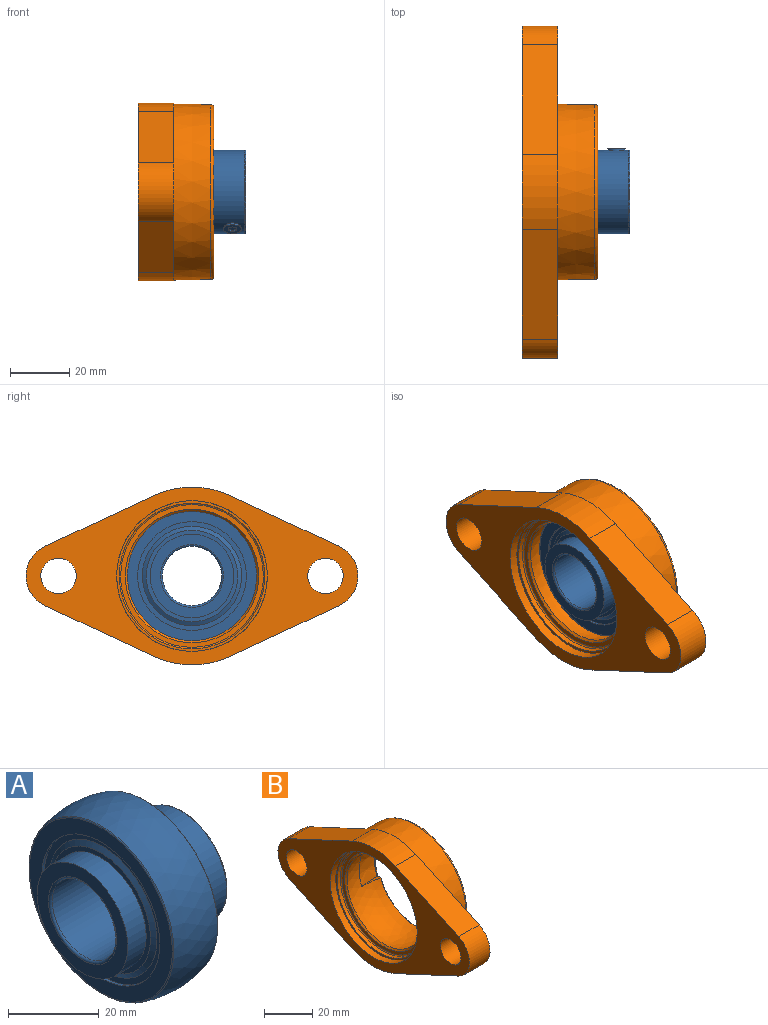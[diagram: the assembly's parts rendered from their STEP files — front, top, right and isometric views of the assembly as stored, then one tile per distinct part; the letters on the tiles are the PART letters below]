
ASSEMBLY  parts=2 mates=1
PART A: 39 faces, bbox 31x48.7x48.7 mm
  f0: cylinder r=3mm len=6mm, axis (0,-0.5,-0.87), area 13.8mm2, adj f15,f21
  f1: plane 30.85x30.85mm, normal (-1,0,0), area 122.9mm2, adj f2,f16
  f2: cone r=16.75mm half-angle=62.2deg, axis (1,0,0), area 151.5mm2, adj f1,f3
  f3: plane 36.68x36.68mm, normal (-1,0,0), area 175mm2, adj f2,f4
  f4: cylinder r=18.34mm len=36.68mm, axis (-1,0,0), area 80.7mm2, adj f3,f5
  f5: plane 44.42x44.42mm, normal (-1,0,0), area 493.5mm2, adj f4,f6
  f6: torus R=22.21mm, axis (1,0,0), area 53.9mm2, adj f5,f7
  f7: sphere r=23.5mm, area 2004.2mm2, adj f6,f8
  f8: torus R=22.21mm, axis (1,0,0), area 53.9mm2, adj f7,f9
  f9: plane 44.42x44.42mm, normal (1,0,0), area 493.5mm2, adj f8,f10
  f10: cylinder r=18.34mm len=36.68mm, axis (-1,0,0), area 80.7mm2, adj f9,f11
  f11: plane 36.68x36.68mm, normal (1,0,0), area 175mm2, adj f10,f12
  f12: cone r=15.42mm half-angle=62.2deg, axis (-1,0,0), area 151.5mm2, adj f11,f13
  f13: plane 30.85x30.85mm, normal (1,0,0), area 122.9mm2, adj f12,f15
  f14: torus R=13.8mm, axis (1,0,0), area 41.4mm2, adj f15,f37
  f15: cylinder r=14.1mm len=28.2mm, axis (-1,0,0), area 911.4mm2, adj f0,f13,f14,f38
  f16: cylinder r=14.1mm len=28.2mm, axis (-1,0,0), area 505mm2, adj f1,f33
  f17: cylinder r=14.1mm len=3mm, axis (-1,0,0), area 7.8mm2, adj f19,f22,f23,f24,f25,f26
  f18: cylinder r=14.1mm len=3.46mm, axis (-1,0,0), area 7.8mm2, adj f27,f28,f29,f30,f31,f32
  f19: plane 1.72x1.24mm, normal (1,0,0), area 0.7mm2, adj f17,f21,f22,f26
  f20: plane 6x6mm, normal (0,1,0), area 20.5mm2, adj f27,f28,f29,f30,f31,f32,f38
  f21: plane 6x5.2mm, normal (0,-0.5,-0.87), area 20.5mm2, adj f0,f19,f22,f23,f24,f25,f26
  f22: plane 1.5x0.97mm, normal (0.5,0.75,-0.43), area 0.8mm2, adj f17,f19,f21,f23
  f23: plane 1.5x0.97mm, normal (-0.5,0.75,-0.43), area 0.8mm2, adj f17,f21,f22,f24
  f24: plane 1.72x1.24mm, normal (-1,0,0), area 0.7mm2, adj f17,f21,f23,f25
  f25: plane 1.5x1.01mm, normal (-0.5,-0.75,0.43), area 0.8mm2, adj f17,f21,f24,f26
  f26: plane 1.5x1.01mm, normal (0.5,-0.75,0.43), area 0.8mm2, adj f17,f19,f21,f25
  f27: plane 1.5x0.87mm, normal (-0.5,0,-0.87), area 0.8mm2, adj f18,f20,f28,f29
  f28: plane 1.5x0.87mm, normal (0.5,0,-0.87), area 0.8mm2, adj f18,f20,f27,f32
  f29: plane 1.73x0.44mm, normal (-1,0,0), area 0.7mm2, adj f18,f20,f27,f30
  f30: plane 1.5x0.87mm, normal (-0.5,0,0.87), area 0.8mm2, adj f18,f20,f29,f31
  f31: plane 1.5x0.87mm, normal (0.5,0,0.87), area 0.8mm2, adj f18,f20,f30,f32
  f32: plane 1.73x0.44mm, normal (1,0,0), area 0.7mm2, adj f18,f20,f28,f31
  f33: plane 28.2x28.2mm, normal (-1,0,0), area 271.6mm2, adj f16,f34
  f34: torus R=10.6mm, axis (1,0,0), area 60.5mm2, adj f33,f35
  f35: cylinder r=10mm len=29.8mm, axis (-1,0,0), area 1872.4mm2, adj f34,f36
  f36: torus R=10.6mm, axis (1,0,0), area 60.5mm2, adj f35,f37
  f37: plane 27.6x27.6mm, normal (1,0,0), area 245.3mm2, adj f14,f36
  f38: cylinder r=3mm len=6mm, axis (0,1,0), area 13.8mm2, adj f15,f20
PART B: 147 faces, bbox 25.5x112x63.8 mm
  f0: plane 10x2.82mm, normal (0,0.34,-0.94), area 13.3mm2, adj f1,f3,f29,f30,f142
  f1: cone r=25.92mm half-angle=5deg, axis (1,0,0), area 169.2mm2, adj f0,f2,f29,f142
  f2: plane 10x2.82mm, normal (0,0.34,0.94), area 13.3mm2, adj f1,f3,f4,f29,f142
  f3: sphere r=23.5mm, area 2370.8mm2, adj f0,f2,f4,f5,f30,f142,f143,f145
  f4: cone r=21.57mm half-angle=45deg, axis (1,0,0), area 51.7mm2, adj f2,f3,f29,f145
  f5: cone r=22.48mm half-angle=45deg, axis (-1,0,0), area 135.7mm2, adj f3,f6
  f6: plane 48.1x48.1mm, normal (-1,0,0), area 230mm2, adj f5,f7
  f7: torus R=24.05mm, axis (1,0,0), area 120.3mm2, adj f6,f8
  f8: cylinder r=24.55mm len=49.1mm, axis (-1,0,0), area 277.7mm2, adj f7,f9
  f9: plane 50.8x50.8mm, normal (-1,0,0), area 133.4mm2, adj f8,f12
  f10: plane 112x60mm, normal (1,0,0), area 1323.8mm2, adj f13,f14,f15,f16,f17,f18,f19,f20
  f11: plane 112x60mm, normal (-1,0,0), area 2151.2mm2, adj f12,f13,f14,f15,f16,f17,f18,f19
  f12: cylinder r=25.4mm len=50.8mm, axis (1,0,0), area 510.7mm2, adj f9,f11
  f13: cylinder r=6mm len=12mm, axis (1,0,0), area 452.4mm2, adj f10,f11
  f14: cylinder r=6mm len=12mm, axis (1,0,0), area 452.4mm2, adj f10,f11
  f15: plane 36.98x17.22mm, normal (0,0.42,0.91), area 489.5mm2, adj f10,f11,f16,f22
  f16: cylinder r=11mm len=19.94mm, axis (1,0,0), area 299.6mm2, adj f10,f11,f15,f17
  f17: plane 36.98x17.22mm, normal (0,0.42,-0.91), area 489.5mm2, adj f10,f11,f16,f18
  f18: cylinder r=30mm len=25.33mm, axis (1,0,0), area 313.8mm2, adj f10,f11,f17,f19
  f19: plane 36.98x17.22mm, normal (0,-0.42,-0.91), area 489.5mm2, adj f10,f11,f18,f20
  f20: cylinder r=11mm len=19.94mm, axis (1,0,0), area 299.6mm2, adj f10,f11,f19,f21
  f21: plane 36.98x17.22mm, normal (0,-0.42,0.91), area 489.5mm2, adj f10,f11,f20,f22
  f22: cylinder r=30mm len=25.33mm, axis (1,0,0), area 313.8mm2, adj f10,f11,f15,f21
  f23: cylinder r=0.25mm len=1mm, axis (1,0,0), area 0.4mm2, adj f10,f24,f60,f61
  f24: plane 1.75x1mm, normal (0,0,-1), area 1.8mm2, adj f10,f23,f31,f61
  f25: cone r=29.47mm half-angle=1deg, axis (-1,0,0), area 2326.9mm2, adj f10,f26
  f26: torus R=28.47mm, axis (1,0,0), area 284.1mm2, adj f25,f27
  f27: plane 56.94x56.94mm, normal (1,0,0), area 638.7mm2, adj f26,f28
  f28: cylinder r=24.64mm len=49.29mm, axis (-1,0,0), area 77.4mm2, adj f27,f29
  f29: plane 49.29x49.29mm, normal (1,0,0), area 276mm2, adj f0,f1,f2,f4,f28,f30,f144,f145
  f30: cone r=21.57mm half-angle=45deg, axis (1,0,0), area 51.7mm2, adj f0,f3,f29,f146
  f31: cylinder r=0.25mm len=1mm, axis (1,0,0), area 0.4mm2, adj f10,f24,f32,f61
  f32: plane 7x1mm, normal (0,1,0), area 7mm2, adj f10,f31,f33,f61
  f33: cylinder r=0.25mm len=1mm, axis (1,0,0), area 0.4mm2, adj f10,f32,f34,f61
  f34: plane 3.25x1mm, normal (0,0,1), area 3.2mm2, adj f10,f33,f35,f61
  f35: cylinder r=0.25mm len=1mm, axis (1,0,0), area 0.4mm2, adj f10,f34,f36,f61
  f36: plane 4x1mm, normal (0,-1,0), area 4mm2, adj f10,f35,f37,f61
  f37: cylinder r=0.25mm len=1mm, axis (1,0,0), area 0.4mm2, adj f10,f36,f38,f61
  f38: plane 1x1mm, normal (0,0,1), area 1mm2, adj f10,f37,f39,f61
  f39: cylinder r=0.25mm len=1mm, axis (1,0,0), area 0.4mm2, adj f10,f38,f40,f61
  f40: plane 1x1mm, normal (0,1,0), area 1mm2, adj f10,f39,f41,f61
  f41: cylinder r=0.25mm len=1mm, axis (1,0,0), area 0.4mm2, adj f10,f40,f42,f61
  f42: plane 1x0.25mm, normal (0,0,-1), area 0.3mm2, adj f10,f41,f43,f61
  f43: cylinder r=0.25mm len=1mm, axis (1,0,0), area 0.4mm2, adj f10,f42,f44,f61
  f44: plane 1.75x1mm, normal (0,1,0), area 1.8mm2, adj f10,f43,f45,f61
  f45: cylinder r=0.25mm len=1mm, axis (1,0,0), area 0.4mm2, adj f10,f44,f46,f61
  f46: plane 1x1mm, normal (0,0,1), area 1mm2, adj f10,f45,f47,f61
  f47: cylinder r=0.25mm len=1mm, axis (1,0,0), area 0.4mm2, adj f10,f46,f48,f61
  f48: plane 5.5x1mm, normal (0,-1,0), area 5.5mm2, adj f10,f47,f49,f61
  f49: cylinder r=0.25mm len=1mm, axis (1,0,0), area 0.4mm2, adj f10,f48,f50,f61
  f50: plane 2.5x1mm, normal (0,0,-1), area 2.5mm2, adj f10,f49,f51,f61
  f51: cylinder r=0.25mm len=1mm, axis (1,0,0), area 0.4mm2, adj f10,f50,f52,f61
  f52: plane 4x1mm, normal (0,1,0), area 4mm2, adj f10,f51,f53,f61
  f53: cylinder r=0.25mm len=1mm, axis (1,0,0), area 0.4mm2, adj f10,f52,f54,f61
  f54: plane 1.75x1mm, normal (0,0,-1), area 1.7mm2, adj f10,f53,f55,f61
  f55: cylinder r=0.25mm len=1mm, axis (1,0,0), area 0.4mm2, adj f10,f54,f56,f61
  f56: plane 2.5x1mm, normal (0,-1,0), area 2.5mm2, adj f10,f55,f57,f61
  f57: cylinder r=0.25mm len=1mm, axis (1,0,0), area 0.4mm2, adj f10,f56,f58,f61
  f58: plane 1x1mm, normal (0,0,1), area 1mm2, adj f10,f57,f59,f61
  f59: cylinder r=0.25mm len=1mm, axis (1,0,0), area 0.4mm2, adj f10,f58,f60,f61
  f60: plane 1.75x1mm, normal (0,-1,0), area 1.8mm2, adj f10,f23,f59,f61
  f61: plane 7.5x6mm, normal (1,0,0), area 28.6mm2, adj f23,f24,f31,f32,f33,f34,f35,f36
  f62: plane 1.9x1mm, normal (0,0,-1), area 1.9mm2, adj f10,f63,f96,f97
  f63: cylinder r=0.25mm len=1mm, axis (1,0,0), area 0.4mm2, adj f10,f62,f64,f97
  f64: plane 2x1mm, normal (0,1,0), area 2mm2, adj f10,f63,f65,f97
  f65: cylinder r=0.25mm len=1mm, axis (1,0,0), area 0.4mm2, adj f10,f64,f66,f97
  f66: plane 2x1mm, normal (0,0,1), area 2mm2, adj f10,f65,f67,f97
  f67: plane 2.18x2.18mm, normal (0,0.71,-0.71), area 3.1mm2, adj f10,f66,f68,f97
  f68: cylinder r=0.25mm len=1mm, axis (1,0,0), area 0.2mm2, adj f10,f67,f69,f97
  f69: plane 2.65x1mm, normal (0,1,0), area 2.6mm2, adj f10,f68,f70,f97
  f70: cylinder r=0.25mm len=1mm, axis (1,0,0), area 0.4mm2, adj f10,f69,f71,f97
  f71: plane 1.75x1mm, normal (0,0,1), area 1.8mm2, adj f10,f70,f72,f97
  f72: cylinder r=0.25mm len=1mm, axis (1,0,0), area 0.4mm2, adj f10,f71,f73,f97
  f73: plane 1.66x1mm, normal (0,-1,0), area 1.7mm2, adj f10,f72,f74,f97
  f74: cylinder r=0.25mm len=1mm, axis (1,0,0), area 0.2mm2, adj f10,f73,f75,f97
  f75: plane 1.68x1.44mm, normal (0,-0.76,0.65), area 2.2mm2, adj f10,f74,f76,f97
  f76: plane 1x0.68mm, normal (0,0.71,0.71), area 1mm2, adj f10,f75,f77,f97
  f77: cylinder r=0.25mm len=1mm, axis (1,0,0), area 0.2mm2, adj f10,f76,f78,f97
  f78: plane 1.9x1mm, normal (0,1,0), area 1.9mm2, adj f10,f77,f79,f97
  f79: cylinder r=0.25mm len=1mm, axis (1,0,0), area 0.4mm2, adj f10,f78,f80,f97
  f80: plane 1x1mm, normal (0,0,1), area 1mm2, adj f10,f79,f81,f97
  f81: cylinder r=0.25mm len=1mm, axis (1,0,0), area 0.4mm2, adj f10,f80,f82,f97
  f82: plane 2.14x1mm, normal (0,-1,0), area 2.1mm2, adj f10,f81,f83,f97
  f83: cylinder r=0.25mm len=1mm, axis (1,0,0), area 0.2mm2, adj f10,f82,f84,f97
  f84: plane 2.17x1.93mm, normal (0,-0.66,-0.75), area 2.9mm2, adj f10,f83,f85,f97
  f85: plane 2x1mm, normal (0,0,1), area 2mm2, adj f10,f84,f86,f97
  f86: cylinder r=0.25mm len=1mm, axis (1,0,0), area 0.4mm2, adj f10,f85,f87,f97
  f87: plane 2x1mm, normal (0,-1,0), area 2mm2, adj f10,f86,f88,f97
  f88: cylinder r=0.25mm len=1mm, axis (1,0,0), area 0.4mm2, adj f10,f87,f89,f97
  f89: plane 1.65x1mm, normal (0,0,-1), area 1.6mm2, adj f10,f88,f90,f97
  f90: cylinder r=0.25mm len=1mm, axis (1,0,0), area 0.2mm2, adj f10,f89,f91,f97
  f91: plane 1x0.1mm, normal (0,0.71,-0.71), area 0.1mm2, adj f10,f90,f92,f97
  f92: cylinder r=0.25mm len=1mm, axis (1,0,0), area 0.2mm2, adj f10,f91,f93,f97
  f93: plane 1.04x1mm, normal (0,0,-1), area 1mm2, adj f10,f92,f94,f97
  f94: cylinder r=0.25mm len=1mm, axis (1,0,0), area 0.2mm2, adj f10,f93,f95,f97
  f95: plane 1x0.1mm, normal (0,-0.71,-0.71), area 0.1mm2, adj f10,f94,f96,f97
  f96: cylinder r=0.25mm len=1mm, axis (1,0,0), area 0.2mm2, adj f10,f62,f95,f97
  f97: plane 7.75x6mm, normal (1,0,0), area 33.3mm2, adj f62,f63,f64,f65,f66,f67,f68,f69
  f98: plane 1.65x1mm, normal (0,0,-1), area 1.6mm2, adj f10,f99,f140,f141
  f99: cylinder r=0.25mm len=1mm, axis (1,0,0), area 0.4mm2, adj f10,f98,f100,f141
  f100: plane 2x1mm, normal (0,1,0), area 2mm2, adj f10,f99,f101,f141
  f101: cylinder r=0.25mm len=1mm, axis (1,0,0), area 0.4mm2, adj f10,f100,f102,f141
  f102: plane 1.75x1mm, normal (0,0,1), area 1.8mm2, adj f10,f101,f103,f141
  f103: cylinder r=0.25mm len=1mm, axis (1,0,0), area 0.4mm2, adj f10,f102,f104,f141
  f104: cylinder r=0.25mm len=1mm, axis (1,0,0), area 0.4mm2, adj f10,f103,f105,f141
  f105: plane 1x0.25mm, normal (0,0,1), area 0.3mm2, adj f10,f104,f106,f141
  f106: cylinder r=0.25mm len=1mm, axis (1,0,0), area 0.4mm2, adj f10,f105,f107,f141
  f107: plane 1x0.9mm, normal (0,1,0), area 0.9mm2, adj f10,f106,f108,f141
  f108: cylinder r=0.25mm len=1mm, axis (1,0,0), area 0.2mm2, adj f10,f107,f109,f141
  f109: plane 1x0.1mm, normal (0,0.71,-0.71), area 0.1mm2, adj f10,f108,f110,f141
  f110: cylinder r=0.25mm len=1mm, axis (1,0,0), area 0.2mm2, adj f10,f109,f111,f141
  f111: plane 1.65x1mm, normal (0,1,0), area 1.6mm2, adj f10,f110,f112,f141
  f112: cylinder r=0.25mm len=1mm, axis (1,0,0), area 0.4mm2, adj f10,f111,f113,f141
  f113: plane 1x0.75mm, normal (0,0,1), area 0.8mm2, adj f10,f112,f114,f141
  f114: cylinder r=0.25mm len=1mm, axis (1,0,0), area 0.4mm2, adj f10,f113,f115,f141
  f115: plane 1.65x1mm, normal (0,-1,0), area 1.6mm2, adj f10,f114,f116,f141
  f116: cylinder r=0.25mm len=1mm, axis (1,0,0), area 0.2mm2, adj f10,f115,f117,f141
  f117: plane 1x0.1mm, normal (0,-0.71,-0.71), area 0.1mm2, adj f10,f116,f118,f141
  f118: cylinder r=0.25mm len=1mm, axis (1,0,0), area 0.2mm2, adj f10,f117,f119,f141
  f119: plane 1x0.9mm, normal (0,-1,0), area 0.9mm2, adj f10,f118,f120,f141
  f120: cylinder r=0.25mm len=1mm, axis (1,0,0), area 0.4mm2, adj f10,f119,f121,f141
  f121: plane 1x1mm, normal (0,0,1), area 1mm2, adj f10,f120,f122,f141
  f122: cylinder r=0.25mm len=1mm, axis (1,0,0), area 0.4mm2, adj f10,f121,f123,f141
  f123: plane 2.25x1mm, normal (0,1,0), area 2.3mm2, adj f10,f122,f124,f141
  f124: cylinder r=0.25mm len=1mm, axis (1,0,0), area 0.4mm2, adj f10,f123,f125,f141
  f125: plane 1x0.25mm, normal (0,0,-1), area 0.3mm2, adj f10,f124,f126,f141
  f126: cylinder r=0.25mm len=1mm, axis (1,0,0), area 0.4mm2, adj f10,f125,f127,f141
  f127: plane 2.5x1mm, normal (0,1,0), area 2.5mm2, adj f10,f126,f128,f141
  f128: cylinder r=0.25mm len=1mm, axis (1,0,0), area 0.4mm2, adj f10,f127,f129,f141
  f129: plane 1x1mm, normal (0,0,1), area 1mm2, adj f10,f128,f130,f141
  f130: cylinder r=0.25mm len=1mm, axis (1,0,0), area 0.4mm2, adj f10,f129,f131,f141
  f131: plane 7.25x1mm, normal (0,-1,0), area 7.3mm2, adj f10,f130,f132,f141
  f132: cylinder r=0.25mm len=1mm, axis (1,0,0), area 0.4mm2, adj f10,f131,f133,f141
  f133: plane 1.65x1mm, normal (0,0,-1), area 1.6mm2, adj f10,f132,f134,f141
  f134: cylinder r=0.25mm len=1mm, axis (1,0,0), area 0.2mm2, adj f10,f133,f135,f141
  f135: plane 1x0.1mm, normal (0,0.71,-0.71), area 0.1mm2, adj f10,f134,f136,f141
  f136: cylinder r=0.25mm len=1mm, axis (1,0,0), area 0.2mm2, adj f10,f135,f137,f141
  f137: plane 1.29x1mm, normal (0,0,-1), area 1.3mm2, adj f10,f136,f138,f141
  f138: cylinder r=0.25mm len=1mm, axis (1,0,0), area 0.2mm2, adj f10,f137,f139,f141
  f139: plane 1x0.1mm, normal (0,-0.71,-0.71), area 0.1mm2, adj f10,f138,f140,f141
  f140: cylinder r=0.25mm len=1mm, axis (1,0,0), area 0.2mm2, adj f10,f98,f139,f141
  f141: plane 7.75x6mm, normal (1,0,0), area 22.9mm2, adj f98,f99,f100,f101,f102,f103,f104,f105
  f142: plane 16.21x1.62mm, normal (1,0,0), area 3.3mm2, adj f0,f1,f2,f3
  f143: plane 16.21x1.62mm, normal (1,0,0), area 3.3mm2, adj f3,f144,f145,f146
  f144: cone r=23.7mm half-angle=5deg, axis (1,0,0), area 169.2mm2, adj f29,f143,f145,f146
  f145: plane 10x2.82mm, normal (0,-0.34,0.94), area 13.3mm2, adj f3,f4,f29,f143,f144
  f146: plane 10x2.82mm, normal (0,-0.34,-0.94), area 13.3mm2, adj f3,f29,f30,f143,f144
PLACE A t=(-32.52,-8.06,18.68)mm
PLACE B t=(-35.52,-8.06,18.68)mm
MATE fastened A.f2 <-> B.f1  axis (1,0,0) through (-25.52,-8.06,18.68)mm
